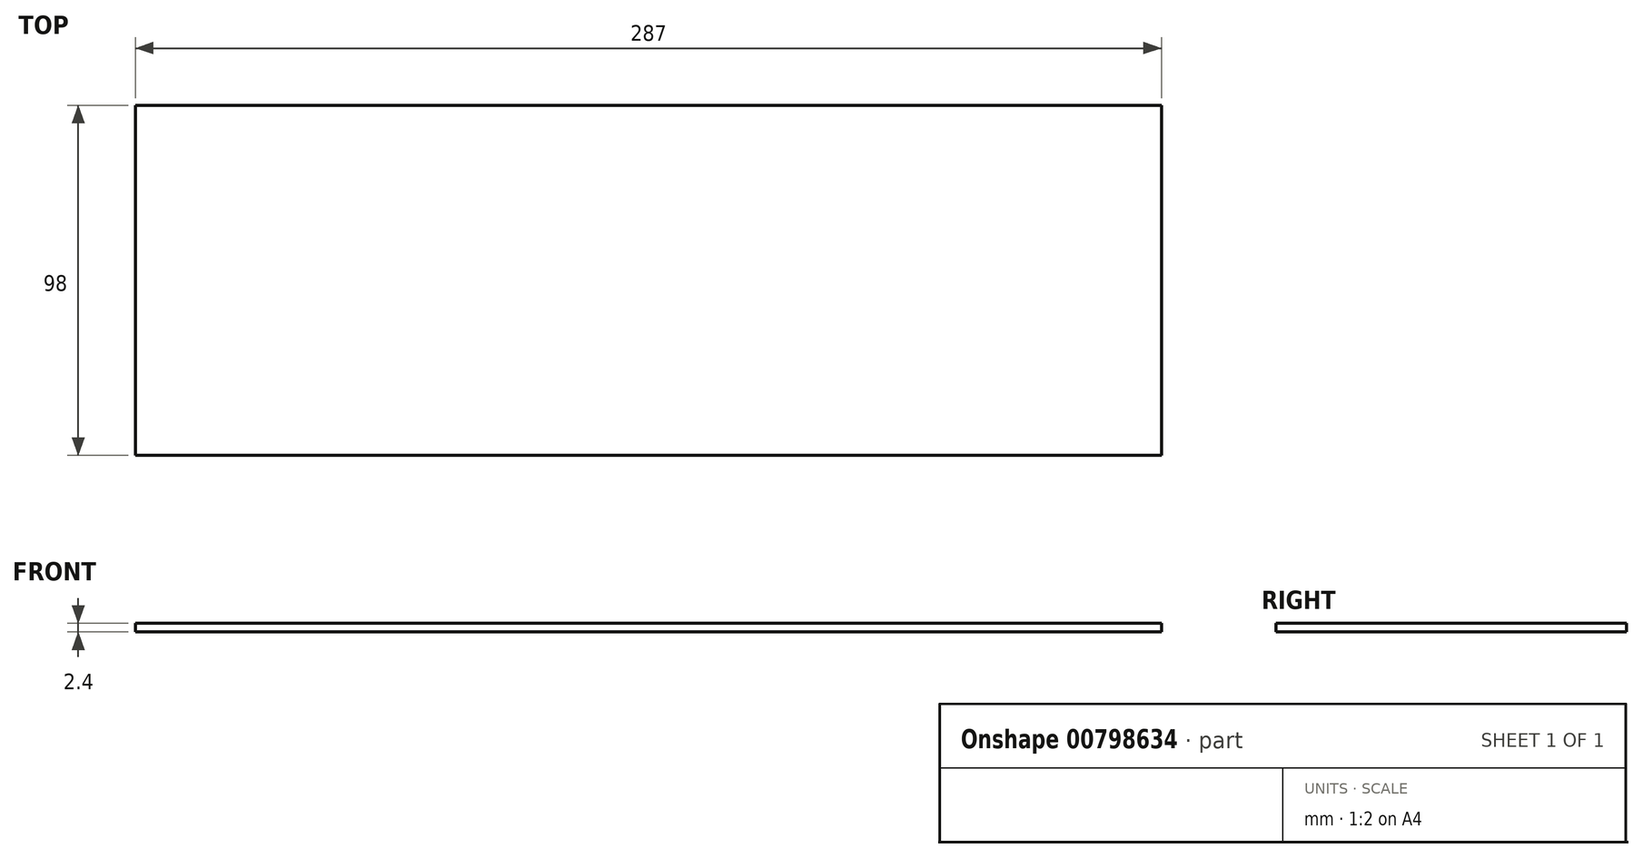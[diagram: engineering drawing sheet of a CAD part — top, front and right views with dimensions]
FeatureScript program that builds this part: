
annotation { "Feature Type Name" : "Feature", "Feature Type Description" : "" }
export const myFeature = defineFeature(function(context is Context, id is Id, definition is map)
    precondition{}
    {
        {
            var Q0;
            Q0=qCreatedBy(makeId("Top.planeOp"),FACE);
            var sketch = newSketch(context, id + "F0", { "sketchPlane" : qUnion([Q0])});
            skLineSegment(sketch, "E0.bottom", {"start": v(-143.5, -49) * mm, "end": v(143.5, -49) * mm});
            skLineSegment(sketch, "E0.top", {"start": v(-143.5, 49) * mm, "end": v(143.5, 49) * mm});
            skLineSegment(sketch, "E0.left", {"start": v(-143.5, -49) * mm, "end": v(-143.5, 49) * mm});
            skLineSegment(sketch, "E0.right", {"start": v(143.5, -49) * mm, "end": v(143.5, 49) * mm});
            skPoint(sketch, "E0.middle", {"position": v(0, 0) * mm});
            skSolve(sketch);
        }
        {
            var Q0;
            Q0=makeQuery(id+"F0.imprint","IMPRINT",FACE,{"disambiguationData":[TD([[makeQuery(id+"F0.imprint","IMPRINT",EDGE,{"derivedFrom":sQuery(id+"F0.wireOp",EDGE,"E0.bottom")}),1.0]])]});
            extrude(context, id + "F1", {"entities" : qUnion([Q0]), "depth" : 2.4 * mm, "offsetDistance" : 25 * mm});
        }
    });
